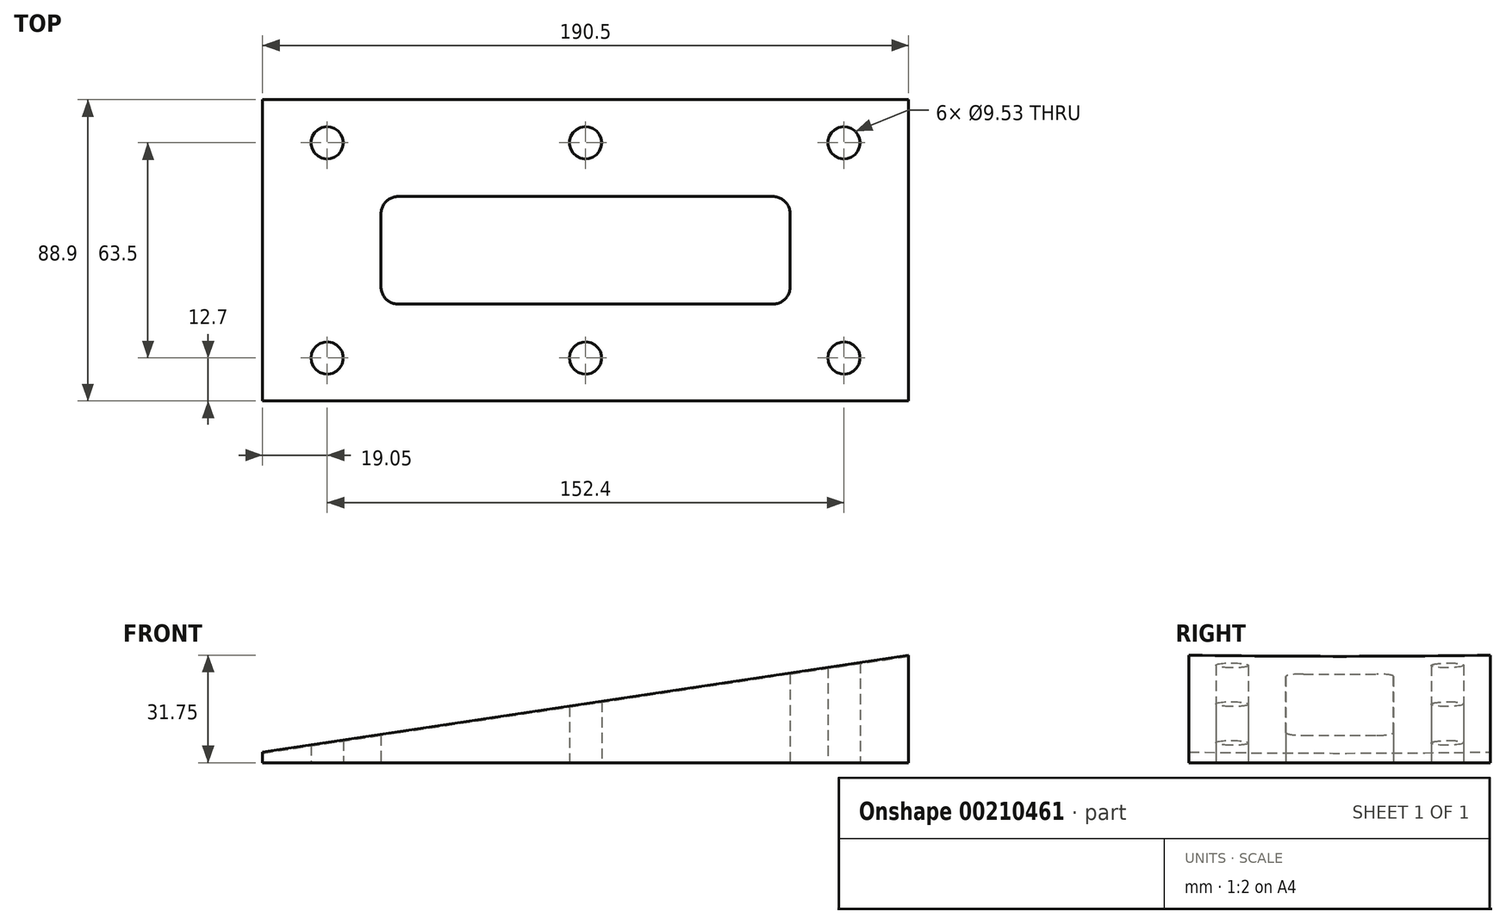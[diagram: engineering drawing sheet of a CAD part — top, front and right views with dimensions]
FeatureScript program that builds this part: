
annotation { "Feature Type Name" : "Feature", "Feature Type Description" : "" }
export const myFeature = defineFeature(function(context is Context, id is Id, definition is map)
    precondition{}
    {
        {
            var Q0;
            Q0=qCreatedBy(makeId("Top.planeOp"),FACE);
            var sketch = newSketch(context, id + "F0", { "sketchPlane" : qUnion([Q0])});
            skLineSegment(sketch, "E0.bottom", {"start": v(-95.25, 44.45) * mm, "end": v(95.25, 44.45) * mm});
            skLineSegment(sketch, "E0.top", {"start": v(-95.25, -44.45) * mm, "end": v(95.25, -44.45) * mm});
            skLineSegment(sketch, "E0.left", {"start": v(-95.25, 44.45) * mm, "end": v(-95.25, -44.45) * mm});
            skLineSegment(sketch, "E0.right", {"start": v(95.25, 44.45) * mm, "end": v(95.25, -44.45) * mm});
            skPoint(sketch, "E0.middle", {"position": v(0, 0) * mm});
            skLineSegment(sketch, "E1.bottom", {"start": v(60.33, 15.88) * mm, "end": v(-60.33, 15.88) * mm});
            skLineSegment(sketch, "E1.top", {"start": v(60.33, -15.87) * mm, "end": v(-60.33, -15.87) * mm});
            skLineSegment(sketch, "E1.left", {"start": v(60.33, 15.88) * mm, "end": v(60.33, -15.87) * mm});
            skLineSegment(sketch, "E1.right", {"start": v(-60.33, 15.88) * mm, "end": v(-60.33, -15.87) * mm});
            skCircle(sketch, "E2", {"center": v(-76.2, 31.75) * mm, "radius": 4.76 * mm});
            skCircle(sketch, "E3", {"center": v(0, 31.75) * mm, "radius": 4.76 * mm});
            skCircle(sketch, "E4", {"center": v(76.2, 31.75) * mm, "radius": 4.76 * mm});
            skCircle(sketch, "E5.MirrorC", {"center": v(76.2, -31.75) * mm, "radius": 4.76 * mm});
            skCircle(sketch, "E6.MirrorC", {"center": v(0, -31.75) * mm, "radius": 4.76 * mm});
            skCircle(sketch, "E7.MirrorC", {"center": v(-76.2, -31.75) * mm, "radius": 4.76 * mm});
            skSolve(sketch);
        }
        {
            var Q0;
            Q0=makeQuery(id+"F0.imprint","IMPRINT",FACE,{"disambiguationData":[TD([[makeQuery(id+"F0.imprint","IMPRINT",EDGE,{"derivedFrom":sQuery(id+"F0.wireOp",EDGE,"E0.bottom")}),-1.0]])]});
            extrude(context, id + "F1", {"entities" : qUnion([Q0]), "depth" : 50.8 * mm});
        }
        {
            var Q0;
            Q0=makeQuery(id+"F1.opExtrude","SWEPT_FACE",FACE,{"disambiguationData":[OSD([sQuery(id+"F0.wireOp",EDGE,"E0.top")])]});
            var sketch = newSketch(context, id + "F2", { "sketchPlane" : qUnion([Q0])});
            skLineSegment(sketch, "E8", {"start": v(-95.25, 3.17) * mm, "end": v(95.25, 31.75) * mm});
            skLineSegment(sketch, "E9", {"start": v(95.25, 31.75) * mm, "end": v(118.78, 86.45) * mm});
            skLineSegment(sketch, "E10", {"start": v(118.78, 86.45) * mm, "end": v(-129.3, 83.84) * mm});
            skLineSegment(sketch, "E11", {"start": v(-129.3, 83.84) * mm, "end": v(-95.25, 3.17) * mm});
            skSolve(sketch);
        }
        {
            var Q0;
            Q0 = qSketchRegion(id + "F2", true);
            extrude(context, id + "F3", {"entities" : qUnion([Q0]), "operationType" : NewBodyOperationType.REMOVE, "endBound" : BoundingType.THROUGH_ALL, "oppositeDirection" : true, "depth" : 25.4 * mm});
        }
        {
            var Q0;
            Q0=makeQuery(id+"F1.opExtrude","SWEPT_FACE",FACE,{"disambiguationData":[OSD([sQuery(id+"F0.wireOp",EDGE,"E0.right")])]});
            var sketch = newSketch(context, id + "F4", { "sketchPlane" : qUnion([Q0])});
            skCircle(sketch, "E12", {"center": v(0, 2927) * mm, "radius": 2895.6 * mm});
            skSolve(sketch);
        }
        {
            var Q0;
            Q0=makeQuery(id+"F1.opExtrude","SWEPT_FACE",FACE,{"disambiguationData":[OSD([sQuery(id+"F0.wireOp",EDGE,"E0.left")])]});
            var sketch = newSketch(context, id + "F5", { "sketchPlane" : qUnion([Q0])});
            skCircle(sketch, "E13", {"center": v(0, 2898.43) * mm, "radius": 2895.6 * mm});
            skSolve(sketch);
        }
        {
            var Q1;
            Q1 = qSketchRegion(id + "F5", true);
            var Q2;
            Q2 = qSketchRegion(id + "F4", true);
            loft(context, id + "F6", {"operationType" : NewBodyOperationType.REMOVE, "sheetProfilesArray" : [{ "sheetProfileEntities" : qUnion([Q1]) }, { "sheetProfileEntities" : qUnion([Q2]) }]});
        }
        {
            var Q0;
            Q0=makeQuery(id+"F1.opExtrude","SWEPT_EDGE",EDGE,{"disambiguationData":[OSD([sQuery(id+"F0.wireOp",EDGE,"E1.bottom"),sQuery(id+"F0.wireOp",EDGE,"E1.left")])]});
            var Q1;
            Q1=makeQuery(id+"F1.opExtrude","SWEPT_EDGE",EDGE,{"disambiguationData":[OSD([sQuery(id+"F0.wireOp",EDGE,"E1.top"),sQuery(id+"F0.wireOp",EDGE,"E1.left")])]});
            var Q2;
            Q2=makeQuery(id+"F1.opExtrude","SWEPT_EDGE",EDGE,{"disambiguationData":[OSD([sQuery(id+"F0.wireOp",EDGE,"E1.top"),sQuery(id+"F0.wireOp",EDGE,"E1.right")])]});
            var Q3;
            Q3=makeQuery(id+"F1.opExtrude","SWEPT_EDGE",EDGE,{"disambiguationData":[OSD([sQuery(id+"F0.wireOp",EDGE,"E1.bottom"),sQuery(id+"F0.wireOp",EDGE,"E1.right")])]});
            fillet(context, id + "F7", {"entities" : qUnion([Q0, Q1, Q2, Q3]), "radius" : 5.08 * mm, "tangentPropagation" : true, "allowEdgeOverflow" : false});
        }
    });
